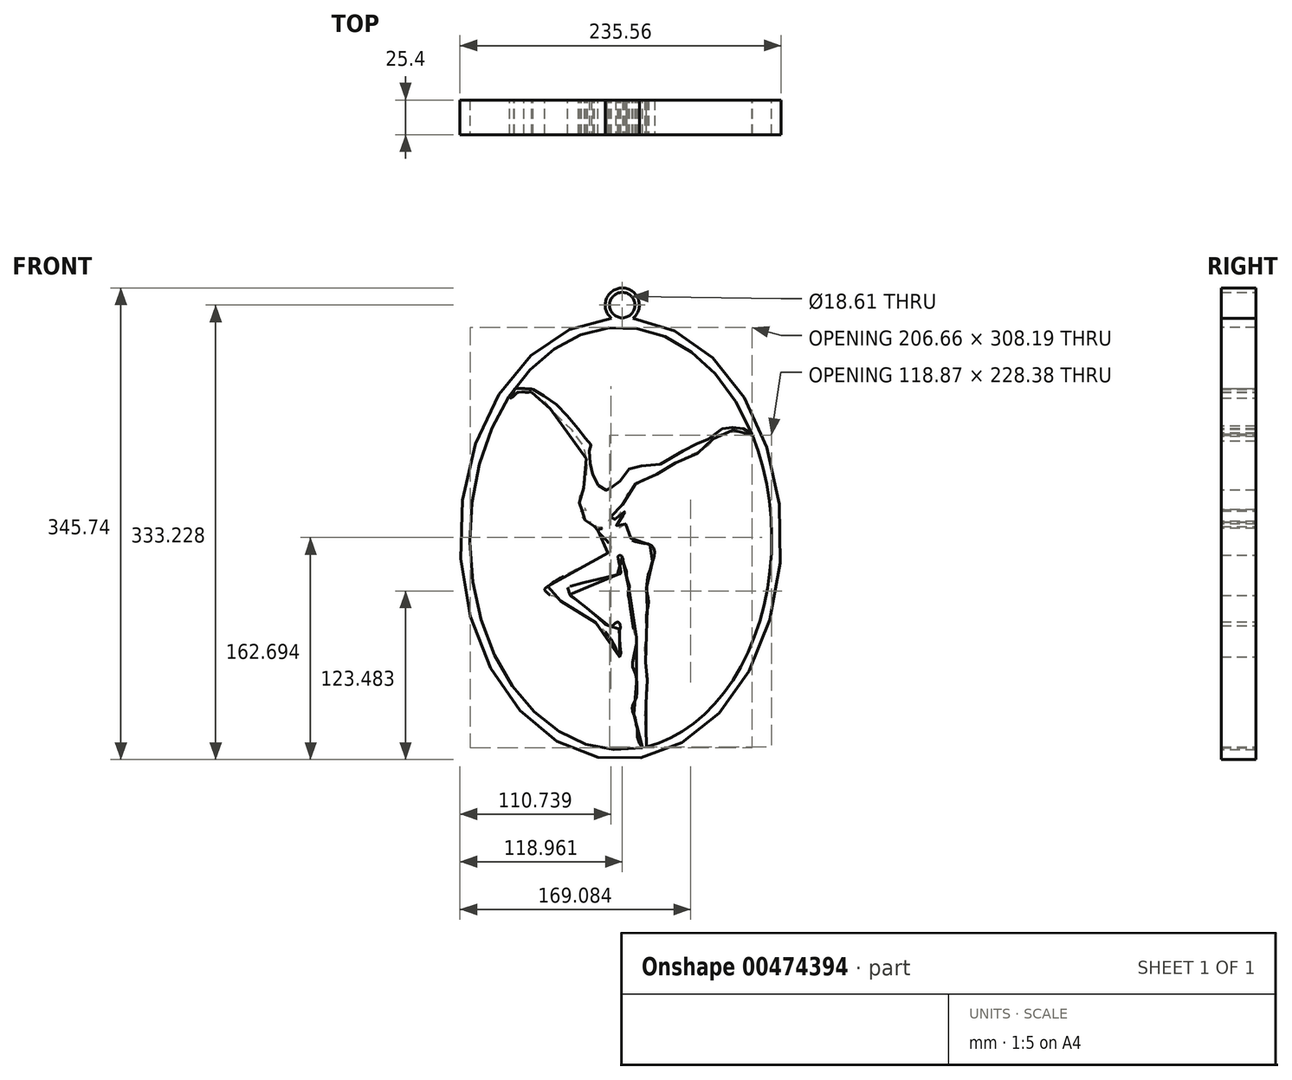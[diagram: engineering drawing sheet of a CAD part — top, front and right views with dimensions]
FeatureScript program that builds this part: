
annotation { "Feature Type Name" : "Feature", "Feature Type Description" : "" }
export const myFeature = defineFeature(function(context is Context, id is Id, definition is map)
    precondition{}
    {
        {
            var Q0;
            Q0=qCreatedBy(makeId("Front.planeOp"),FACE);
            var sketch = newSketch(context, id + "F0", { "sketchPlane" : qUnion([Q0])});
            skPoint(sketch, "E0.253.internal.snap0", {"position": v(24.75, 296.74) * mm});
            skPoint(sketch, "E0.259.internal.snap0", {"position": v(24.75, 296.74) * mm});
            skPoint(sketch, "E0.263.internal.snap0", {"position": v(24.75, 296.74) * mm});
            skPoint(sketch, "E0.280.internal.snap0", {"position": v(24.75, 296.74) * mm});
            skPoint(sketch, "E0.286.internal.snap0", {"position": v(24.75, 296.74) * mm});
            skFitSpline(sketch, "E0", {"points": [v(37.93, 26.35) * mm, v(41.64, 17.22) * mm, v(44.02, 17.35) * mm, v(45.6, 18.94) * mm, v(44.94, 21.58) * mm, v(44.15, 24.5) * mm, v(44.55, 28.06) * mm, v(44.15, 32.7) * mm, v(43.49, 37.19) * mm, v(43.49, 41.15) * mm, v(44.02, 44.86) * mm, v(44.41, 54.75) * mm, v(44.68, 62.29) * mm, v(45.62, 63.9) * mm, v(45.62, 65.79) * mm, v(45.09, 67.4) * mm, v(44.28, 69.42) * mm, v(45.22, 71.84) * mm, v(44.41, 74.8) * mm, v(44.14, 77.63) * mm, v(44, 81.4) * mm, v(43.5, 89.4) * mm, v(43.98, 95.43) * mm, v(44.78, 100.76) * mm, v(44.87, 105.28) * mm, v(44.78, 111.67) * mm, v(45.05, 118.06) * mm, v(46.11, 121.52) * mm, v(46.1, 124.45) * mm, v(45.78, 127.92) * mm, v(45, 132.03) * mm, v(44.83, 136.46) * mm, v(45.57, 142.3) * mm, v(47.53, 148.33) * mm, v(49.35, 154.79) * mm, v(50.34, 157.31) * mm, v(50.76, 160.54) * mm, v(50.06, 163.63) * mm, v(48.23, 165.59) * mm, v(44.72, 166.71) * mm, v(40.66, 167.27) * mm, v(37.29, 168.11) * mm, v(34.62, 168.96) * mm, v(32.52, 172.6) * mm, v(31.86, 175.63) * mm, v(30.97, 176.53) * mm, v(30.08, 178.02) * mm, v(30.18, 179.6) * mm, v(29.88, 181.1) * mm, v(28.59, 181.3) * mm, v(27.9, 180.5) * mm, v(26.8, 179.6) * mm, v(25.5, 178.61) * mm, v(23.72, 178.12) * mm, v(22.33, 178.51) * mm, v(22.62, 180.1) * mm, v(24.21, 181.2) * mm, v(25.5, 182.49) * mm, v(27.4, 185.07) * mm, v(28.19, 187.45) * mm, v(28.68, 189.54) * mm, v(28.49, 191.23) * mm, v(27.2, 191.63) * mm, v(26, 190.53) * mm, v(24.41, 188.55) * mm, v(23.22, 186.66) * mm, v(21.63, 184.67) * mm, v(19.74, 183.58) * mm, v(17.96, 183.28) * mm, v(16.27, 183.88) * mm, v(15.47, 184.67) * mm, v(16.96, 185.57) * mm, v(17.96, 185.96) * mm, v(19.45, 187.36) * mm, v(21.33, 188.65) * mm, v(22.92, 190.53) * mm, v(25, 193.12) * mm, v(26.2, 194.7) * mm, v(27.6, 196.1) * mm, v(27.4, 197.49) * mm, v(27.3, 199.18) * mm, v(29.18, 201.36) * mm, v(37.71, 211.66) * mm, v(42.56, 214.01) * mm, v(45.15, 214.3) * mm, v(49.4, 216.07) * mm, v(53.28, 218.72) * mm, v(57.17, 220.84) * mm, v(60, 221.9) * mm, v(63.19, 224.56) * mm, v(67.08, 226.33) * mm, v(71.5, 228.8) * mm, v(75.21, 230.92) * mm, v(80.7, 232.16) * mm, v(84.19, 235.33) * mm, v(86.51, 237.97) * mm, v(89.58, 238.5) * mm, v(91.6, 241.57) * mm, v(95.83, 245.48) * mm, v(99.95, 247.92) * mm, v(105.56, 247.39) * mm, v(107.89, 249.93) * mm, v(110.53, 250.56) * mm, v(114.24, 249.08) * mm, v(118.05, 245.8) * mm, v(122.28, 245.8) * mm, v(121.75, 247.5) * mm, v(118.79, 248.98) * mm, v(116.14, 250.99) * mm, v(112.65, 253) * mm, v(107.89, 252.15) * mm, v(103.76, 250.77) * mm, v(100.59, 251.2) * mm, v(98.9, 250.25) * mm, v(87.15, 242) * mm, v(83.45, 241.68) * mm, v(79.85, 238.71) * mm, v(75.72, 237.13) * mm, v(55.1, 225.23) * mm, v(53.67, 224.73) * mm, v(36.52, 223.4) * mm, v(33.68, 222.47) * mm, v(31.75, 221.22) * mm, v(29.83, 218.2) * mm, v(21.88, 209.17) * mm, v(20.8, 208.58) * mm, v(19.37, 208.42) * mm, v(18.29, 208.25) * mm, v(17.45, 207.41) * mm, v(16.61, 206.5) * mm, v(14.6, 206) * mm, v(13.01, 206.66) * mm, v(10.17, 208.58) * mm, v(7.34, 213.46) * mm, v(5.35, 217.13) * mm, v(3.97, 220.8) * mm, v(3.44, 225.82) * mm, v(2.87, 233.28) * mm, v(2.71, 234.88) * mm, v(3.6, 236.09) * mm, v(4.4, 237.7) * mm, v(4.16, 239.05) * mm, v(3.28, 240.34) * mm, v(1.83, 240.9) * mm, v(0, 244.17) * mm, v(-2.72, 247.64) * mm, v(-6.27, 252.12) * mm, v(-12.1, 259.3) * mm, v(-19.28, 266.57) * mm, v(-22.33, 270.12) * mm, v(-29.62, 274.65) * mm, v(-35.5, 278.57) * mm, v(-38.56, 279.98) * mm, v(-39.79, 279.86) * mm, v(-39.97, 278.88) * mm, v(-39.36, 277.4) * mm, v(-37.52, 275.33) * mm, v(-35.69, 274.28) * mm, v(-33.17, 273.49) * mm, v(-32.44, 273.06) * mm, v(-31.46, 272.2) * mm, v(-29.38, 269.7) * mm, v(-26.99, 266.81) * mm, v(-7.96, 247.62) * mm, v(-1.22, 237.63) * mm, v(-0.53, 236.2) * mm, v(1.54, 220.23) * mm, v(1.2, 218.87) * mm, v(0, 217.4) * mm, v(-0.58, 216.35) * mm, v(-0.56, 213.18) * mm, v(-0.5, 210.24) * mm, v(-1.04, 208.16) * mm, v(-1.96, 206.99) * mm, v(-2.97, 205.65) * mm, v(-3.74, 203.91) * mm, v(-4.03, 203.05) * mm, v(-3.36, 202.47) * mm, v(-3.07, 201.8) * mm, v(-3.45, 201.22) * mm, v(-4.58, 201) * mm, v(-5.2, 200.07) * mm, v(-4.85, 197.97) * mm, v(-4.34, 195.8) * mm, v(-3.33, 194.65) * mm, v(-2.47, 194.46) * mm, v(-1.31, 194.36) * mm, v(-0.42, 193.79) * mm, v(0, 193.19) * mm, v(0.35, 192.38) * mm, v(0.31, 191.56) * mm, v(0, 191.1) * mm, v(-0.89, 190.9) * mm, v(-1.7, 191.06) * mm, v(-2.67, 191.56) * mm, v(-3.28, 191.83) * mm, v(-3.9, 191.6) * mm, v(-4.45, 191.14) * mm, v(-4.33, 190.4) * mm, v(-3.83, 189.9) * mm, v(-3.67, 189.36) * mm, v(-3.63, 188.43) * mm, v(-3.75, 187.97) * mm, v(-2.94, 186.8) * mm, v(-2.12, 185.84) * mm, v(-1.12, 185.06) * mm, v(-0.42, 184.33) * mm, v(0.55, 183.6) * mm, v(1.63, 183.05) * mm, v(3.02, 182.7) * mm, v(3.87, 182.7) * mm, v(5.19, 182.74) * mm, v(6.12, 182.66) * mm, v(6.62, 182) * mm, v(6.47, 181.5) * mm, v(6, 181.23) * mm, v(5.7, 181) * mm, v(5.58, 180.5) * mm, v(5.73, 179.88) * mm, v(6.78, 179.3) * mm, v(7.86, 179.26) * mm, v(8.83, 179.3) * mm, v(9.64, 179.18) * mm, v(12.42, 179.1) * mm, v(16.33, 178.68) * mm, v(9.64, 177.44) * mm, v(9.02, 176.98) * mm, v(9.06, 176.05) * mm, v(9.52, 175.04) * mm, v(10.18, 174.5) * mm, v(17.3, 167.03) * mm, v(18.5, 165.36) * mm, v(18.6, 163.6) * mm, v(18.05, 161.56) * mm, v(16.93, 160.45) * mm, v(10.54, 156.1) * mm, v(-13.45, 144.52) * mm, v(-28.83, 134.7) * mm, v(-29.85, 133.58) * mm, v(-29.58, 132.29) * mm, v(-27.82, 130.62) * mm, v(-25.5, 128.86) * mm, v(-24.2, 128.77) * mm, v(-21.89, 127.75) * mm, v(-19.02, 125.37) * mm, v(-13.8, 122.28) * mm, v(-9.4, 120.07) * mm, v(-4.44, 116.53) * mm, v(3.95, 111.85) * mm, v(11.38, 105.4) * mm, v(17.65, 98.15) * mm, v(22.83, 88.34) * mm, v(23.28, 86.08) * mm, v(24.75, 83.94) * mm, v(25.77, 84.84) * mm, v(25.67, 89.33) * mm, v(25.09, 97.06) * mm, v(25.17, 98.97) * mm, v(24.94, 99.9) * mm, v(24.75, 101.72) * mm, v(25.1, 104.25) * mm, v(25.57, 106.02) * mm, v(25.44, 107.66) * mm, v(24.75, 108.8) * mm, v(23.96, 109.38) * mm, v(22.72, 109.14) * mm, v(21.74, 108.48) * mm, v(20.95, 107.69) * mm, v(20.08, 107.03) * mm, v(18.18, 106.68) * mm, v(16.14, 106.84) * mm, v(14.3, 107.98) * mm, v(-2.3, 122.18) * mm, v(-10.5, 128.17) * mm, v(-11.65, 129.3) * mm, v(-12, 130.88) * mm, v(-12.22, 132.16) * mm, v(-12.93, 133.16) * mm, v(-13.15, 134.09) * mm, v(-12.3, 135.01) * mm, v(24.75, 144.34) * mm, v(25.8, 144.82) * mm, v(26.04, 145.79) * mm, v(25.88, 147.16) * mm, v(23.87, 156.24) * mm, v(24.05, 157.96) * mm, v(24.75, 158.36) * mm, v(25.83, 158.16) * mm, v(26.98, 156.84) * mm, v(27.69, 153.94) * mm, v(28.1, 151.1) * mm, v(29.97, 146.64) * mm, v(30.24, 141.4) * mm, v(32.2, 135.97) * mm, v(31.13, 130.18) * mm, v(31.45, 128.2) * mm, v(32.46, 123.33) * mm, v(36.23, 99.9) * mm, v(37.6, 97.43) * mm, v(34.35, 78.2) * mm, v(34.91, 75.65) * mm, v(36.75, 70.85) * mm, v(37.45, 65.9) * mm, v(37.74, 59.69) * mm, v(37.03, 53.33) * mm, v(34.65, 48.4) * mm, v(34.25, 46.48) * mm, v(34.65, 43.45) * mm, v(35.86, 40.61) * mm, v(36.67, 38.59) * mm, v(36.98, 34.64) * mm, v(38, 31) * mm, v(37.93, 26.35) * mm]});
            skFitSpline(sketch, "E1", {"points": [v(-55.24, 273.68) * mm, v(-53.8, 273.98) * mm, v(-50.41, 277.46) * mm, v(-49.94, 277.84) * mm, v(-45.06, 278.1) * mm, v(-44, 278.78) * mm, v(-44.04, 279.86) * mm, v(-44.84, 280.55) * mm, v(-50.74, 280.58) * mm, v(-51.49, 280.77) * mm, v(-51.96, 280.52) * mm, v(-52.32, 279.86) * mm, v(-52.29, 279.22) * mm, v(-52.48, 278.48) * mm, v(-52.9, 277.65) * mm, v(-53.25, 276.85) * mm, v(-54.22, 275.66) * mm, v(-55.57, 274.64) * mm, v(-55.24, 273.68) * mm]});
            skFitSpline(sketch, "E2", {"points": [v(-44.84, 280.55) * mm, v(-43.57, 280.3) * mm, v(-42.27, 280.22) * mm, v(-40.5, 280.3) * mm, v(-38.56, 279.98) * mm], "startDerivative": vector(5.62, -1.22) * mm, "endDerivative": vector(6.93, -1.59) * mm});
            skFitSpline(sketch, "E3", {"points": [v(-45.06, 278.1) * mm, v(-43.57, 277.73) * mm, v(-42.27, 277.7) * mm, v(-40.5, 278.1) * mm, v(-39.58, 277.78) * mm], "startDerivative": vector(5.84, -1.55) * mm, "endDerivative": vector(3.92, -2.24) * mm});
            skSolve(sketch);
        }
        {
            var Q0;
            {var subQ0=sQuery(id+"F0.wireOp",EDGE,"E2");Q0=makeQuery(id+"F0.imprint","IMPRINT",FACE,{"disambiguationData":[TD([[makeQuery(id+"F0.imprint","IMPRINT",EDGE,{"derivedFrom":subQ0}),-1.0]])]});}
            var Q1;
            {var subQ0=sQuery(id+"F0.wireOp",EDGE,"E1");var subQ1=makeQuery(id+"F0.imprint","INTERSECT",VERTEX,{"derivedFrom":[subQ0,sQuery(id+"F0.wireOp",EDGE,"E2")]});Q1=makeQuery(id+"F0.imprint","IMPRINT",FACE,{"disambiguationData":[TD([[makeQuery(id+"F0.imprint","IMPRINT",EDGE,{"disambiguationData":[TD([[subQ1,1.0]])],"derivedFrom":subQ0}),1.0]])]});}
            var Q2;
            {var subQ0=sQuery(id+"F0.wireOp",EDGE,"E0");var subQ1=makeQuery(id+"F0.imprint","INTERSECT",VERTEX,{"derivedFrom":[subQ0,sQuery(id+"F0.wireOp",EDGE,"E2")]});Q2=makeQuery(id+"F0.imprint","IMPRINT",FACE,{"disambiguationData":[TD([[makeQuery(id+"F0.imprint","IMPRINT",EDGE,{"disambiguationData":[TD([[subQ1,-1.0]])],"derivedFrom":subQ0}),1.0]])]});}
            extrude(context, id + "F1", {"entities" : qUnion([Q0, Q1, Q2]), "depth" : 25.4 * mm, "offsetDistance" : 25.4 * mm});
        }
        {
            var Q0;
            Q0=qCreatedBy(makeId("Front.planeOp"),FACE);
            var sketch = newSketch(context, id + "F2", { "sketchPlane" : qUnion([Q0])});
            skEllipse(sketch, "E4", {"center": v(25.77, 170.5) * mm, "majorRadius": 154.94 * mm, "minorRadius": 110.8 * mm, "majorAxis": v(0, 1)});
            skEllipse(sketch, "E5", {"center": v(25.77, 170.5) * mm, "majorRadius": 161.93 * mm, "minorRadius": 117.78 * mm, "majorAxis": v(0, 1)});
            skSolve(sketch);
        }
        {
            var Q0;
            Q0 = qSketchRegion(id + "F2", true);
            extrude(context, id + "F3", {"entities" : qUnion([Q0]), "operationType" : NewBodyOperationType.ADD, "depth" : 25.4 * mm, "offsetDistance" : 25.4 * mm});
        }
        {
            var Q0;
            Q0=qCreatedBy(makeId("Front.planeOp"),FACE);
            var sketch = newSketch(context, id + "F4", { "sketchPlane" : qUnion([Q0])});
            skCircle(sketch, "E6", {"center": v(26.95, 341.8) * mm, "radius": 12.52 * mm});
            skCircle(sketch, "E7", {"center": v(26.95, 341.8) * mm, "radius": 9.3 * mm});
            skSolve(sketch);
        }
        {
            var Q0;
            Q0=makeQuery(id+"F4.imprint","IMPRINT",FACE,{"disambiguationData":[TD([[makeQuery(id+"F4.imprint","IMPRINT",EDGE,{"derivedFrom":sQuery(id+"F4.wireOp",EDGE,"E6")}),1.0]])]});
            extrude(context, id + "F5", {"entities" : qUnion([Q0]), "operationType" : NewBodyOperationType.ADD, "depth" : 25.4 * mm, "offsetDistance" : 25.4 * mm});
        }
    });
